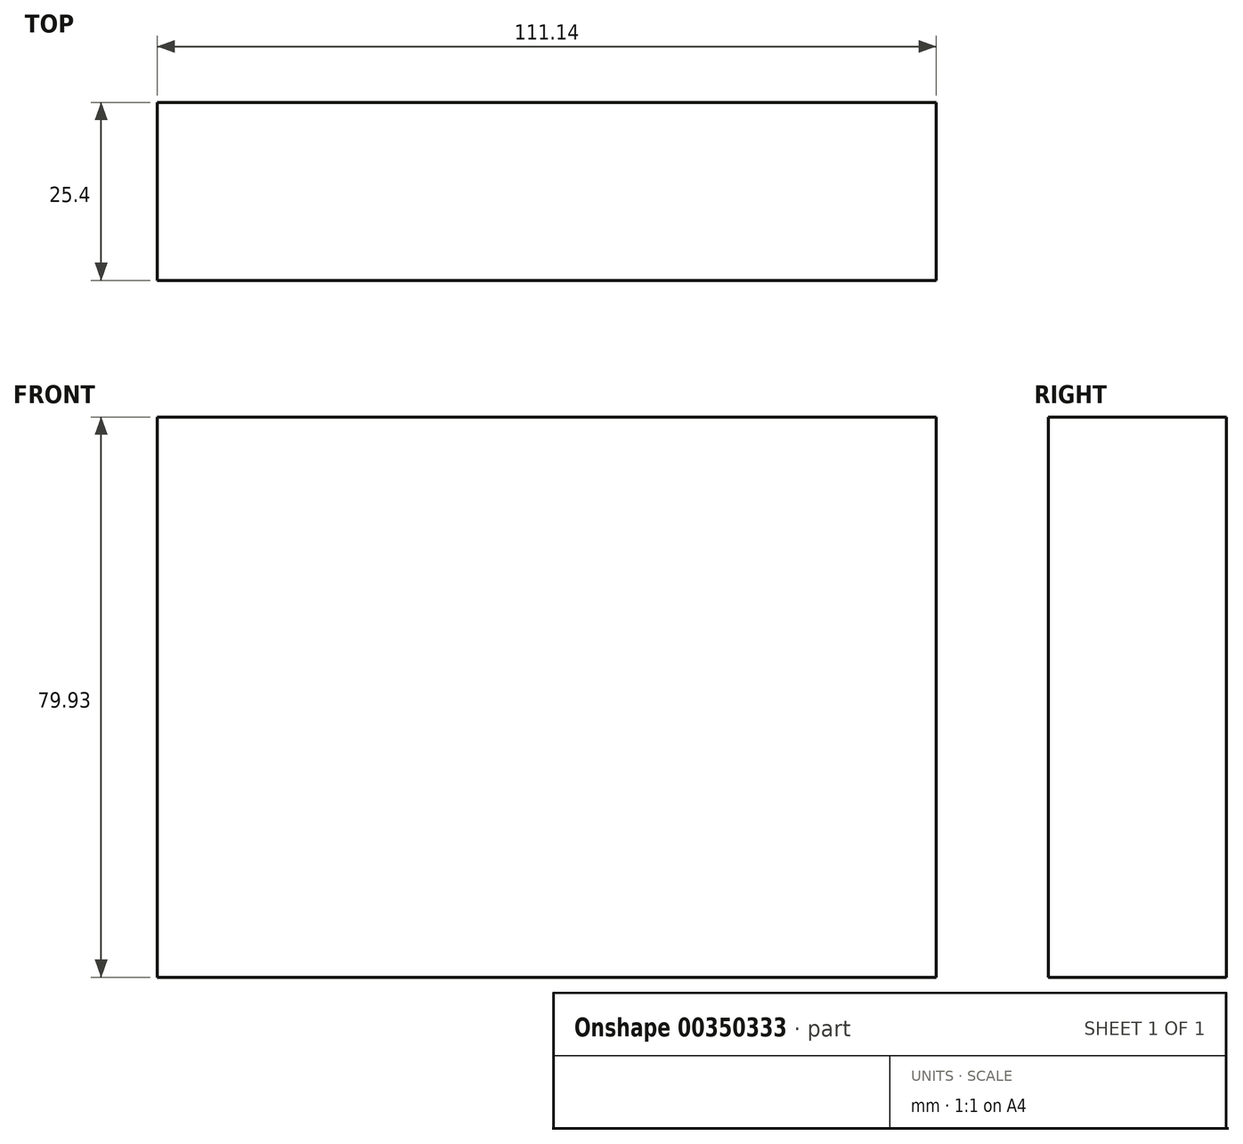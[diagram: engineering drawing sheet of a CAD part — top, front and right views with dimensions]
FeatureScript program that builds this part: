
annotation { "Feature Type Name" : "Feature", "Feature Type Description" : "" }
export const myFeature = defineFeature(function(context is Context, id is Id, definition is map)
    precondition{}
    {
        {
            var Q0;
            Q0=qCreatedBy(makeId("Front.planeOp"),FACE);
            var sketch = newSketch(context, id + "F0", { "sketchPlane" : qUnion([Q0])});
            skLineSegment(sketch, "E0.bottom", {"start": v(0, 0) * mm, "end": v(111.14, 0) * mm});
            skLineSegment(sketch, "E0.top", {"start": v(0, 79.93) * mm, "end": v(111.14, 79.93) * mm});
            skLineSegment(sketch, "E0.left", {"start": v(0, 0) * mm, "end": v(0, 79.93) * mm});
            skLineSegment(sketch, "E0.right", {"start": v(111.14, 0) * mm, "end": v(111.14, 79.93) * mm});
            skSolve(sketch);
        }
        {
            var Q0;
            Q0=makeQuery(id+"F0.imprint","IMPRINT",FACE,{"disambiguationData":[TD([[makeQuery(id+"F0.imprint","IMPRINT",EDGE,{"derivedFrom":sQuery(id+"F0.wireOp",EDGE,"E0.bottom")}),1.0]])]});
            extrude(context, id + "F1", {"entities" : qUnion([Q0]), "depth" : 25.4 * mm});
        }
    });
